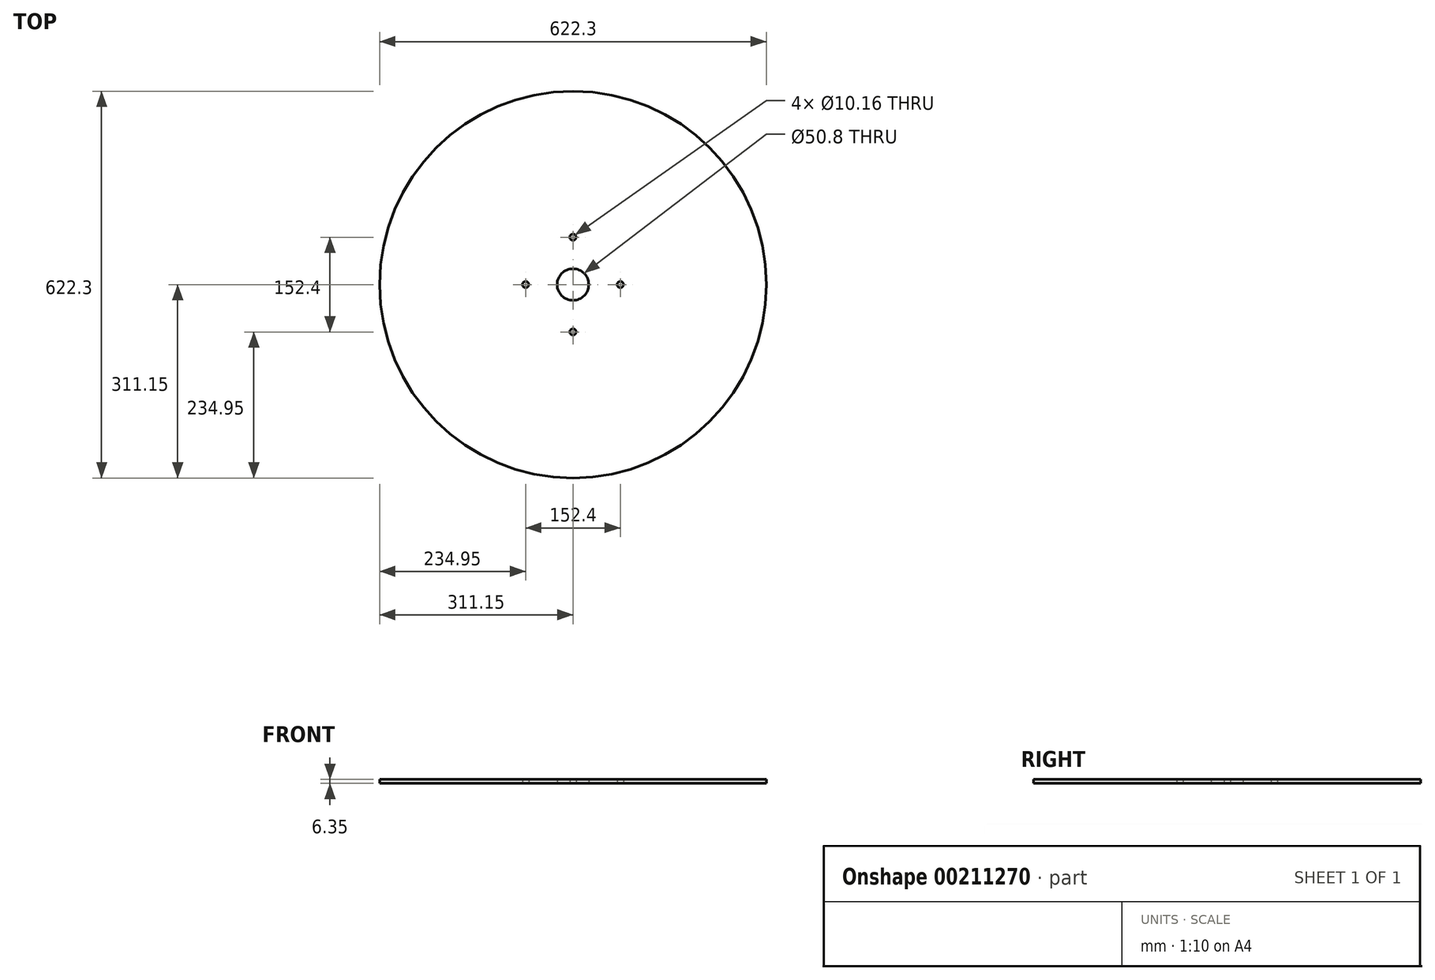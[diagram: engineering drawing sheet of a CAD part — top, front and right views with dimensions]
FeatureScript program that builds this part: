
annotation { "Feature Type Name" : "Feature", "Feature Type Description" : "" }
export const myFeature = defineFeature(function(context is Context, id is Id, definition is map)
    precondition{}
    {
        {
            var Q0;
            Q0=qCreatedBy(makeId("Top.planeOp"),FACE);
            var sketch = newSketch(context, id + "F0", { "sketchPlane" : qUnion([Q0])});
            skCircle(sketch, "E0", {"center": v(0, 0) * mm, "radius": 311.15 * mm});
            skCircle(sketch, "E1", {"center": v(0, 0) * mm, "radius": 25.4 * mm});
            skCircle(sketch, "E2", {"center": v(0, 76.2) * mm, "radius": 5.08 * mm});
            skCircle(sketch, "E3.1.0", {"center": v(-76.2, 0) * mm, "radius": 5.08 * mm});
            skCircle(sketch, "E3.2.0", {"center": v(0, -76.2) * mm, "radius": 5.08 * mm});
            skCircle(sketch, "E3.3.0", {"center": v(76.2, 0) * mm, "radius": 5.08 * mm});
            skSolve(sketch);
        }
        {
            var Q0;
            Q0 = qSketchRegion(id + "F0", true);
            extrude(context, id + "F1", {"entities" : qUnion([Q0]), "depth" : 6.35 * mm});
        }
    });
